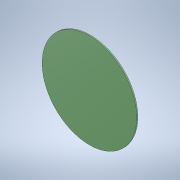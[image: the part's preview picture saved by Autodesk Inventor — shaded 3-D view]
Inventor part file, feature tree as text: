
AUTODESK INVENTOR PART (.ipt)
format: ipt  version: 2020.4 (Build 244396000, 396)  size: 95,744 bytes
history: native  units: mm
features: extrude x1, sketch x1
ambient origin geometry x8: Origin, YZ Plane, XZ Plane, XY Plane, X Axis, Y Axis, Z Axis, Center Point
bodies: Solid1 (feature_tree)
feature tree (2):
  extrude  "Extrusion1"  Depth=0.5mm TaperAngle=0.0deg
  sketch  "Sketch1"  dims[d0=45.0mm d1=0.5mm d2=0.0mm]
